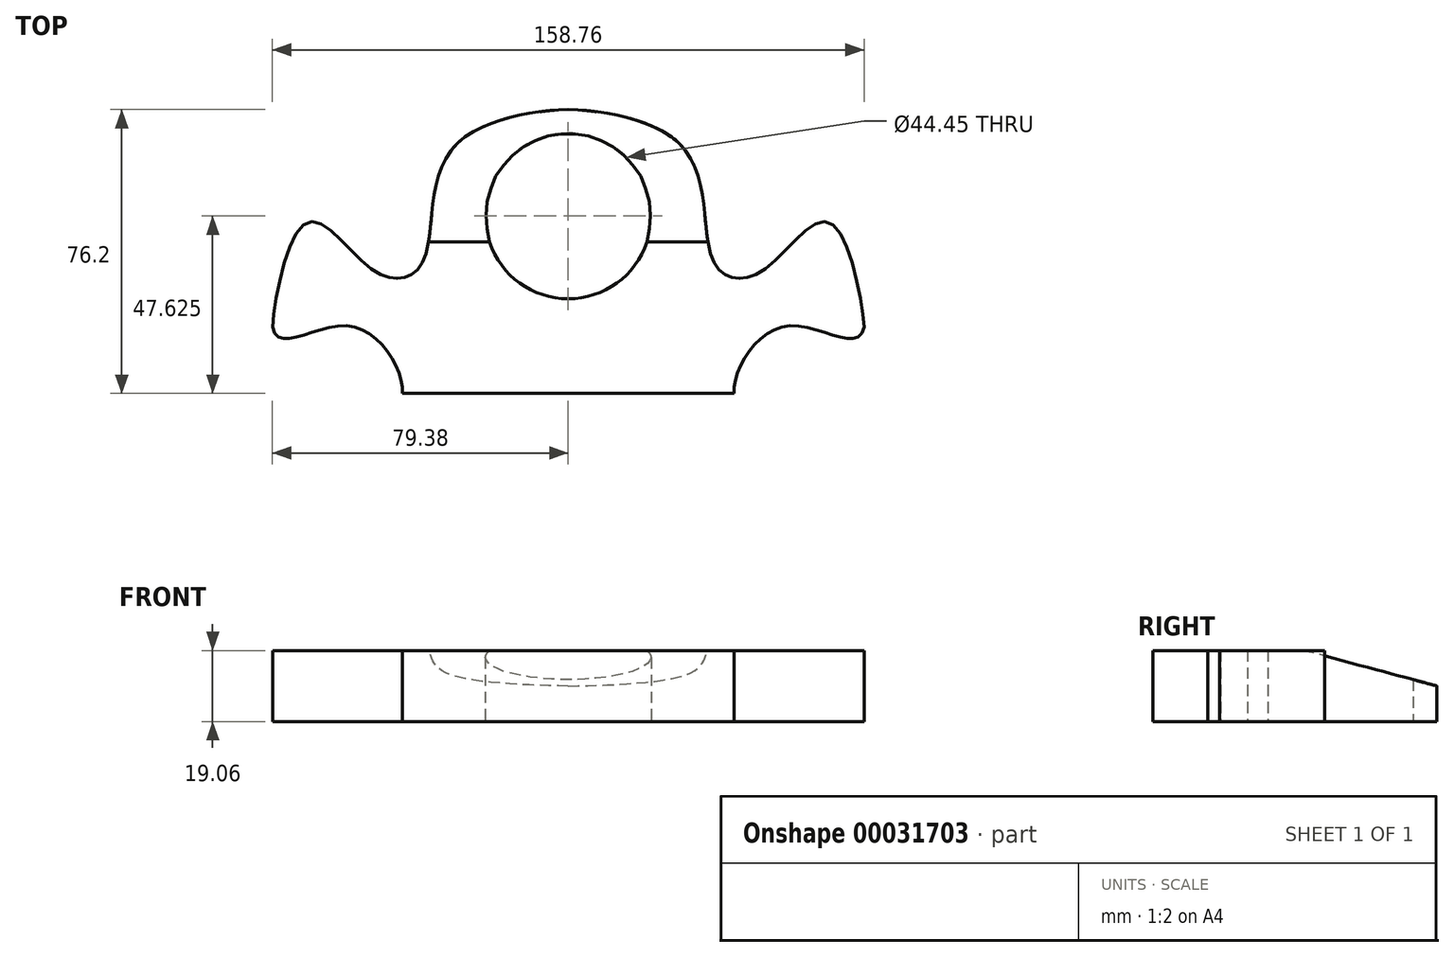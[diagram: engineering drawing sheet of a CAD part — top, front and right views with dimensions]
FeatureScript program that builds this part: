
annotation { "Feature Type Name" : "Feature", "Feature Type Description" : "" }
export const myFeature = defineFeature(function(context is Context, id is Id, definition is map)
    precondition{}
    {
        {
            var Q0;
            Q0=qCreatedBy(makeId("Top.planeOp"),FACE);
            var sketch = newSketch(context, id + "F0", { "sketchPlane" : qUnion([Q0])});
            skLineSegment(sketch, "E0.rect.bottom", {"start": v(79.38, 38.1) * mm, "end": v(-79.38, 38.1) * mm});
            skLineSegment(sketch, "E0.rect.top", {"start": v(79.38, -38.1) * mm, "end": v(-79.38, -38.1) * mm});
            skLineSegment(sketch, "E0.rect.left", {"start": v(79.37, 38.1) * mm, "end": v(79.38, -38.1) * mm});
            skLineSegment(sketch, "E0.rect.right", {"start": v(-79.38, 38.1) * mm, "end": v(-79.37, -38.1) * mm});
            skPoint(sketch, "E0.rect.middle", {"position": v(0, 0) * mm});
            skCircle(sketch, "E1", {"center": v(0, 9.53) * mm, "radius": 22.23 * mm});
            skPoint(sketch, "E2", {"position": v(44.45, -38.1) * mm});
            skPoint(sketch, "E3", {"position": v(79.38, -20.26) * mm});
            skPoint(sketch, "E4.MirrorP", {"position": v(-79.38, -20.26) * mm});
            skFitSpline(sketch, "E5", {"points": [v(44.45, -38.1) * mm, v(59.56, -19.94) * mm, v(79.38, -20.26) * mm], "startDerivative": vector(-1.63, 37.82) * mm, "endDerivative": vector(9.1, 47.36) * mm});
            skFitSpline(sketch, "E6.MirrorCS", {"points": [v(-44.45, -38.1) * mm, v(-59.56, -19.94) * mm, v(-79.38, -20.26) * mm], "startDerivative": vector(1.63, 37.82) * mm, "endDerivative": vector(-9.1, 47.36) * mm});
            skFitSpline(sketch, "E7", {"points": [v(0, 38.1) * mm, v(-29.94, 28.84) * mm, v(-37.98, 0) * mm, v(-43.78, -6.9) * mm, v(-53.93, -3.84) * mm, v(-70.03, 7.76) * mm, v(-79.38, -20.26) * mm], "startDerivative": vector(-66, 0) * mm, "endDerivative": vector(-7.94, -107.5) * mm});
            skFitSpline(sketch, "E8.MirrorCS", {"points": [v(0, 38.1) * mm, v(29.94, 28.84) * mm, v(37.98, 0) * mm, v(43.78, -6.9) * mm, v(53.93, -3.84) * mm, v(70.03, 7.76) * mm, v(79.38, -20.26) * mm], "startDerivative": vector(66, 0) * mm, "endDerivative": vector(7.94, -107.5) * mm});
            skLineSegment(sketch, "E9", {"start": v(-79.38, 38.1) * mm, "end": v(79.38, 38.1) * mm});
            skPoint(sketch, "E10", {"position": v(0, -13.1) * mm});
            skPoint(sketch, "E11", {"position": v(104.56, 3.58) * mm});
            skSolve(sketch);
        }
        {
            var Q0;
            Q0=makeQuery(id+"F0.imprint","IMPRINT",FACE,{"disambiguationData":[TD([[makeQuery(id+"F0.imprint","IMPRINT",EDGE,{"derivedFrom":sQuery(id+"F0.wireOp",EDGE,"E1")}),-1.0]])]});
            extrude(context, id + "F1", {"entities" : qUnion([Q0]), "endBound" : BoundingType.SYMMETRIC, "depth" : 19.05 * mm});
        }
        {
            var Q0;
            Q0=sQuery(id+"F0.wireOp",EDGE,"E9");
            cPlane(context, id + "F2", {"entities" : qUnion([Q0]), "cplaneType" : CPlaneType.LINE_ANGLE, "offset" : 152.4 * mm, "angle" : 75 * degree, "width" : 152.4 * mm, "height" : 152.4 * mm});
        }
        {
            var Q0;
            Q0=qCreatedBy(id+"F2.planeOp",FACE);
            var sketch = newSketch(context, id + "F3", { "sketchPlane" : qUnion([Q0])});
            skLineSegment(sketch, "E12.rect.bottom", {"start": v(-58.9, 51.09) * mm, "end": v(58.9, 51.09) * mm});
            skLineSegment(sketch, "E12.rect.top", {"start": v(-58.9, -51.09) * mm, "end": v(58.9, -51.09) * mm});
            skLineSegment(sketch, "E12.rect.left", {"start": v(-58.9, 51.09) * mm, "end": v(-58.9, -51.09) * mm});
            skLineSegment(sketch, "E12.rect.right", {"start": v(58.9, 51.09) * mm, "end": v(58.9, -51.09) * mm});
            skPoint(sketch, "E12.rect.middle", {"position": v(0, 0) * mm});
            skSolve(sketch);
        }
        {
            var Q0;
            Q0=makeQuery(id+"F3.imprint","IMPRINT",FACE,{"disambiguationData":[TD([[makeQuery(id+"F3.imprint","IMPRINT",EDGE,{"derivedFrom":sQuery(id+"F3.wireOp",EDGE,"E12.rect.bottom")}),-1.0]])]});
            extrude(context, id + "F4", {"entities" : qUnion([Q0]), "operationType" : NewBodyOperationType.REMOVE, "depth" : 12.7 * mm});
        }
    });
